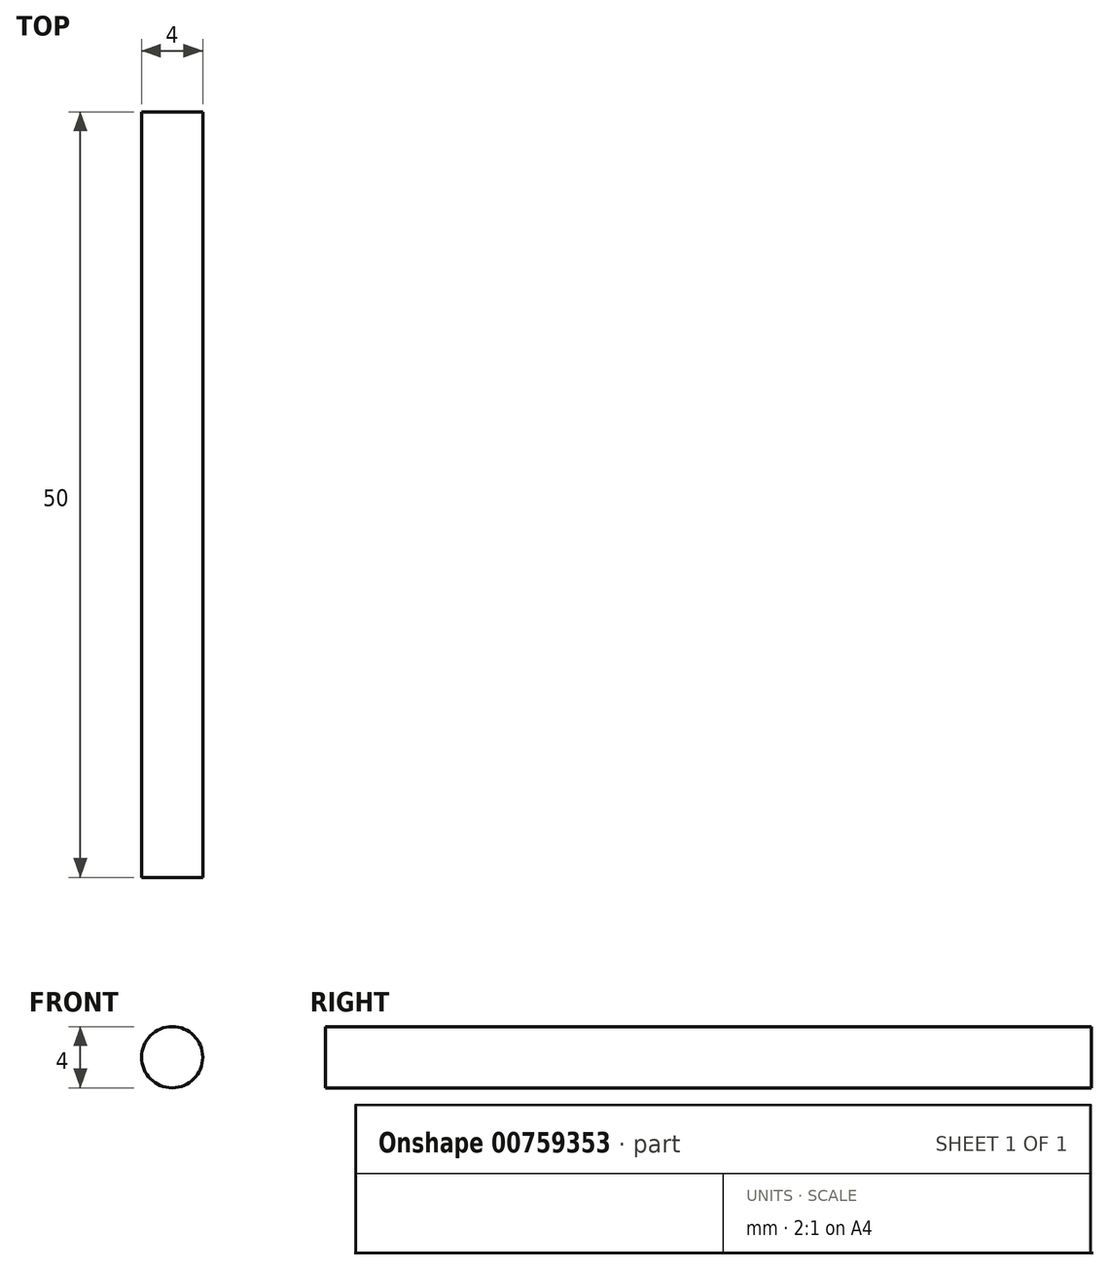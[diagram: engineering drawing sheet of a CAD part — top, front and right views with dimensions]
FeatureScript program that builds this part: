
annotation { "Feature Type Name" : "Feature", "Feature Type Description" : "" }
export const myFeature = defineFeature(function(context is Context, id is Id, definition is map)
    precondition{}
    {
        {
            var Q0;
            Q0=qCreatedBy(makeId("Front.planeOp"),FACE);
            var sketch = newSketch(context, id + "F0", { "sketchPlane" : qUnion([Q0])});
            skCircle(sketch, "E0", {"center": v(0, 0) * mm, "radius": 2 * mm});
            skSolve(sketch);
        }
        {
            var Q0;
            Q0=makeQuery(id+"F0.imprint","IMPRINT",FACE,{"disambiguationData":[TD([[makeQuery(id+"F0.imprint","IMPRINT",EDGE,{"derivedFrom":sQuery(id+"F0.wireOp",EDGE,"E0")}),1.0]])]});
            extrude(context, id + "F1", {"entities" : qUnion([Q0]), "depth" : 50 * mm, "offsetDistance" : 25 * mm});
        }
    });
